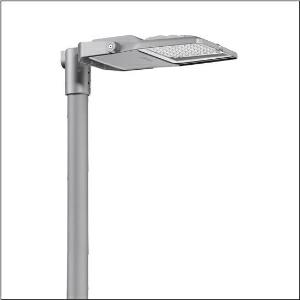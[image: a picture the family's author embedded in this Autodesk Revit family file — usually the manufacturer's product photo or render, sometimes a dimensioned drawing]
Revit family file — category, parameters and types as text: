
# Revit family: floodlight_fl_21_mini___pl33t_5xa7775b2f3a_d5fa
name_source: partatom
category: Lighting Fixtures
units: mm (PartAtom-declared; Revit-internal decimal feet)

## family parameters
Cut with Voids When Loaded = No
Host = Face
Light Source = No
Part Type = Normal
Room Calculation Point = No
Round Connector Dimension = Use Diameter
Shared = No

## types (1)
- --- (1 x LED, 6150 lm, 45.7 W, 3000K)
    Apparent Load = 46 VA
    CIE Flux Codes = 26 75 99 100 100
    Color Rendering = 70
    Color Temperature = 3000K
    Default Elevation = 1800 mm
    Description = Floodlight FL 21 mini, floodlight, primary light control with lens, of PMMA, primary optical cover: protective disc, of toughened safety glass, transparent, light distribution: PL33T, light emission: direct distribution, installation type: surface-mounted, LED, High Power LED, rated luminous flux: 6.150lm, luminous efficacy: 135lm/W, light colour: 730, colour temperature: 3000K, control gear: Smart Interface (Zhaga), control: flexible luminous flux parameterisation, time-dependent luminous flux control, constant luminous flux control, overheat protection, pre-setting: logarithmic dimming characteristic, with terminal, 6-pole, mains connection: 220..240V, AC, 50/60Hz, start of lifetime: 46W, end of service life: 48W, reduction: 22W, luminaire housing, of diecast aluminium, powder-coated, SITECO metallic grey (DB 702S), corrosivity category C5 mid according to DIN EN ISO 12944, suitable for swimming pools, chlorine-resistant, sealing non-destructively replaceable, please order mast flange separately, mast bracket, of steel, galvanised, powder-coated, SITECO metallic grey (DB 702S), Smart Interface above, protection rating (complete): IP66, insulation class (complete): insulation class II (safety insulation), certification: CE, ENEC, VDE, protection symbol: D, impact resistance: IK08, permissible operating ambient temperature: -40..+40°C, permissible operating ambient temperature for outdoor applications: -40..+50°C, standard: DIN EN 12944, LABS conformity tested according to VDMA 24364:2018-05, packaging unit: 1 piece

Light Distribution: PL33T
    Height = 70 mm
    Lamp = 1 x LED
    Lamp Light Flux = 6150 lm
    Lamp Power = 45.7 W
    Lamp count = 1
    Length = 485 mm
    Luminous efficacy = 135 lm/W
    Manufacturer = Siteco
    ModVariant = No
    Model = 5XA7775B2F3A
    Mounting Place = Pole
    Mounting Type = Pole annexe
    Number of Poles = 1
    OnlyDefault = Yes
    Power Factor = 1
    Product Name = Floodlight FL 21 mini | PL33T
    Product group = floodlight | pylon annexe
    ProductGroupID = 6201
    Protection Class = Protection class II
    Protection Degree = IP 66
    RLX_Detail_Level = 1
    RLX_Emergency_Light_Flux = 0 lm
    RLX_Emergency_Type = 0
    RLX_Emergency_Type_DB = No
    RlxData = <blob elided: 100937 chars, md5=77b476c7>
    Socket = socket
    Standby Power = 0 W
    System Light Flux = 6150 lm
    System Power = 46 W
    Type Comments = factory setting: luminous flux: 100 % | dim-lin: 254 | 463 mA
    Type Image = l_1007125.jpg
    URL = http://relux.com
    VarID = @adj_149725
    Voltage = 0 V
    Weight = 0.00 kg
    Width = 337 mm

## geometry (parser evidence)
native form markers: Blend x4, Sweep x12
no freeform markers — native parametric forms only
